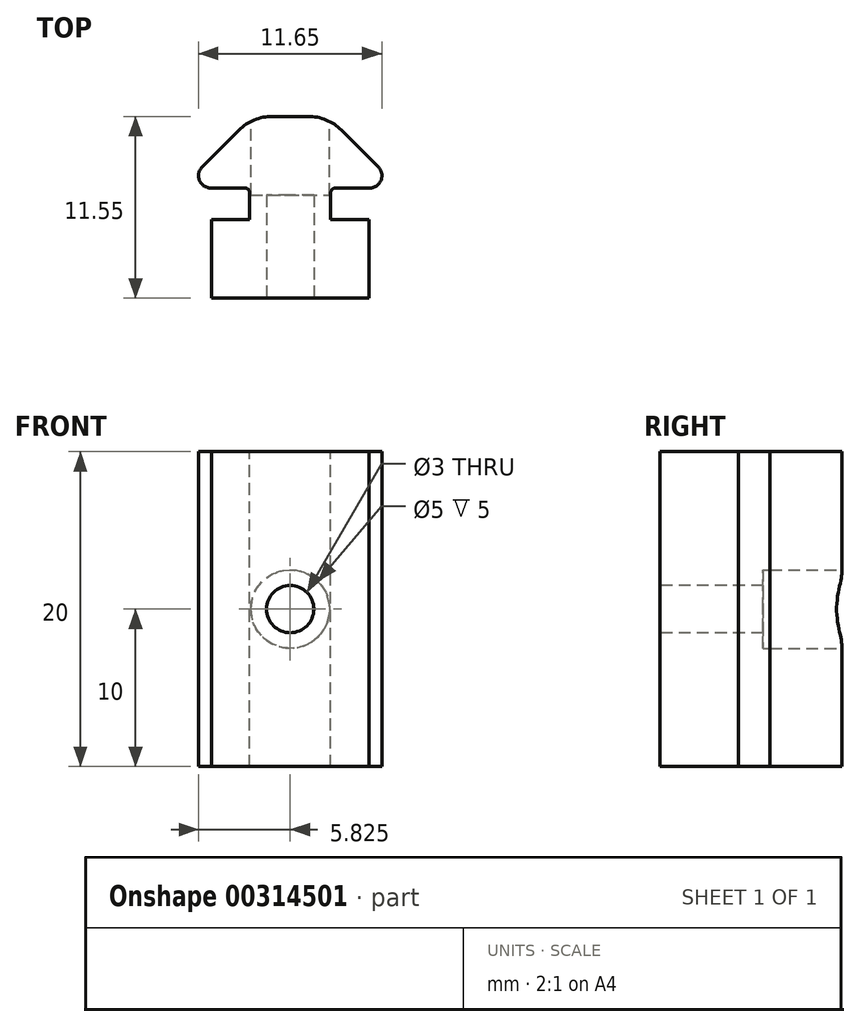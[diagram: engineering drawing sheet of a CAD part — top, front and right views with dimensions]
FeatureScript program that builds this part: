
annotation { "Feature Type Name" : "Feature", "Feature Type Description" : "" }
export const myFeature = defineFeature(function(context is Context, id is Id, definition is map)
    precondition{}
    {
        {
            var Q0;
            Q0=qCreatedBy(makeId("Top.planeOp"),FACE);
            var sketch = newSketch(context, id + "F0", { "sketchPlane" : qUnion([Q0])});
            skLineSegment(sketch, "E0.0.13", {"start": v(-0.8, -19.2) * mm, "end": v(-0.8, -18.5) * mm});
            skArc(sketch, "E0.0.14", {"start": v(-0.8, -18.5) * mm, "mid": v(-0.71, -18.29) * mm, "end": v(-0.5, -18.2) * mm});
            skLineSegment(sketch, "E0.0.15", {"start": v(-0.5, -18.2) * mm, "end": v(1.67, -18.2) * mm});
            skArc(sketch, "E0.0.16", {"start": v(1.67, -18.2) * mm, "mid": v(2.39, -17.72) * mm, "end": v(2.22, -16.87) * mm});
            skLineSegment(sketch, "E0.0.17", {"start": v(2.22, -16.87) * mm, "end": v(-0.12, -14.53) * mm});
            skArc(sketch, "E0.0.18", {"start": v(-0.12, -14.53) * mm, "mid": v(-1.1, -13.88) * mm, "end": v(-2.24, -13.65) * mm});
            skLineSegment(sketch, "E0.0.19", {"start": v(-2.24, -13.65) * mm, "end": v(-4.5, -13.65) * mm});
            skArc(sketch, "E0.0.20", {"start": v(-4.5, -13.65) * mm, "mid": v(-5.66, -13.88) * mm, "end": v(-6.63, -14.53) * mm});
            skLineSegment(sketch, "E0.0.21", {"start": v(-6.63, -14.53) * mm, "end": v(-8.97, -16.87) * mm});
            skArc(sketch, "E0.0.22", {"start": v(-8.97, -16.87) * mm, "mid": v(-9.14, -17.72) * mm, "end": v(-8.42, -18.2) * mm});
            skLineSegment(sketch, "E0.0.23", {"start": v(-8.42, -18.2) * mm, "end": v(-6.25, -18.2) * mm});
            skArc(sketch, "E0.0.24", {"start": v(-6.25, -18.2) * mm, "mid": v(-6.04, -18.29) * mm, "end": v(-5.95, -18.5) * mm});
            skLineSegment(sketch, "E0.0.25", {"start": v(-5.95, -18.5) * mm, "end": v(-5.95, -19.2) * mm});
            skLineSegment(sketch, "E1", {"start": v(-3.38, -13.65) * mm, "end": v(-3.38, -28.6) * mm, "construction": true});
            skLineSegment(sketch, "E2", {"start": v(-5.95, -19.2) * mm, "end": v(-5.95, -20.2) * mm});
            skLineSegment(sketch, "E3", {"start": v(-5.95, -20.2) * mm, "end": v(-8.38, -20.2) * mm});
            skLineSegment(sketch, "E4", {"start": v(-8.38, -20.2) * mm, "end": v(-8.38, -25.2) * mm});
            skLineSegment(sketch, "E5", {"start": v(-8.38, -25.2) * mm, "end": v(-3.38, -25.2) * mm});
            skLineSegment(sketch, "E6.MirrorCS", {"start": v(1.62, -25.2) * mm, "end": v(-3.38, -25.2) * mm});
            skLineSegment(sketch, "E7.MirrorCS", {"start": v(1.62, -20.2) * mm, "end": v(1.62, -25.2) * mm});
            skLineSegment(sketch, "E8.MirrorCS", {"start": v(-0.8, -19.2) * mm, "end": v(-0.8, -20.2) * mm});
            skLineSegment(sketch, "E9.MirrorCS", {"start": v(-0.8, -20.2) * mm, "end": v(1.62, -20.2) * mm});
            skSolve(sketch);
        }
        {
            var Q0;
            Q0=qSketchRegion(id+"F0",true);
            extrude(context, id + "F1", {"entities" : qUnion([Q0]), "oppositeDirection" : true, "depth" : 60 * mm});
        }
        {
            var Q0;
            Q0=makeQuery(id+"F1.opExtrude","SWEPT_FACE",FACE,{"disambiguationData":[OSD([sQuery(id+"F0.wireOp",EDGE,"E5"),sQuery(id+"F0.wireOp",EDGE,"E6.MirrorCS")])]});
            var sketch = newSketch(context, id + "F2", { "sketchPlane" : qUnion([Q0])});
            skLineSegment(sketch, "E10", {"start": v(-3.38, 0) * mm, "end": v(-3.38, -60) * mm, "construction": true});
            skCircle(sketch, "E11", {"center": v(-3.38, -50) * mm, "radius": 1.5 * mm});
            skCircle(sketch, "E12", {"center": v(-3.38, -30) * mm, "radius": 1.5 * mm});
            skCircle(sketch, "E13", {"center": v(-3.38, -10) * mm, "radius": 1.5 * mm});
            skSolve(sketch);
        }
        {
            var Q0;
            Q0=qSketchRegion(id+"F2",true);
            extrude(context, id + "F3", {"entities" : qUnion([Q0]), "operationType" : NewBodyOperationType.REMOVE, "oppositeDirection" : true, "depth" : 25 * mm});
        }
        {
            var Q0;
            Q0=makeQuery(id+"F3.boolean.opBoolean","SPLIT",FACE,{"disambiguationData":[TD([makeQuery(id+"F1.opExtrude","SWEPT_FACE",FACE,{"disambiguationData":[OSD([sQuery(id+"F0.wireOp",EDGE,"E0.0.18")])]}),makeQuery(id+"F1.opExtrude","SWEPT_FACE",FACE,{"disambiguationData":[OSD([sQuery(id+"F0.wireOp",EDGE,"E0.0.20")])]}),makeQuery(id+"F3.opExtrude","SWEPT_FACE",FACE,{"disambiguationData":[OSD([sQuery(id+"F2.wireOp",EDGE,"E12")])]}),makeQuery(id+"F3.opExtrude","SWEPT_FACE",FACE,{"disambiguationData":[OSD([sQuery(id+"F2.wireOp",EDGE,"E13")])]})])],"derivedFrom":makeQuery(id+"F1.opExtrude","SWEPT_FACE",FACE,{"disambiguationData":[OSD([sQuery(id+"F0.wireOp",EDGE,"E0.0.19")])]})});
            var sketch = newSketch(context, id + "F4", { "sketchPlane" : qUnion([Q0])});
            skCircle(sketch, "E14", {"center": v(3.38, -10) * mm, "radius": 2.5 * mm});
            skCircle(sketch, "E15", {"center": v(3.38, -30) * mm, "radius": 2.5 * mm});
            skSolve(sketch);
        }
        {
            var Q0;
            {var subQ0=sQuery(id+"F0.wireOp",EDGE,"E0.0.20");var subQ1=sQuery(id+"F0.wireOp",EDGE,"E0.0.19");var subQ2=sQuery(id+"F0.wireOp",EDGE,"E0.0.18");Q0=makeQuery(id+"F3.boolean.opBoolean","SPLIT",FACE,{"disambiguationData":[TD([makeQuery(id+"F1.opExtrude","CAP_FACE",FACE,{"disambiguationData":[OSD([sQuery(id+"F0.wireOp",EDGE,"E0.0.13"),sQuery(id+"F0.wireOp",EDGE,"E0.0.14"),sQuery(id+"F0.wireOp",EDGE,"E0.0.15"),sQuery(id+"F0.wireOp",EDGE,"E0.0.16"),sQuery(id+"F0.wireOp",EDGE,"E0.0.17"),subQ2,subQ1,subQ0,sQuery(id+"F0.wireOp",EDGE,"E0.0.21"),sQuery(id+"F0.wireOp",EDGE,"E0.0.22"),sQuery(id+"F0.wireOp",EDGE,"E0.0.23"),sQuery(id+"F0.wireOp",EDGE,"E0.0.24"),sQuery(id+"F0.wireOp",EDGE,"E0.0.25"),sQuery(id+"F0.wireOp",EDGE,"E2"),sQuery(id+"F0.wireOp",EDGE,"E3"),sQuery(id+"F0.wireOp",EDGE,"E4"),sQuery(id+"F0.wireOp",EDGE,"E5"),sQuery(id+"F0.wireOp",EDGE,"E6.MirrorCS"),sQuery(id+"F0.wireOp",EDGE,"E7.MirrorCS"),sQuery(id+"F0.wireOp",EDGE,"E8.MirrorCS"),sQuery(id+"F0.wireOp",EDGE,"E9.MirrorCS")])],"isStart":false}),makeQuery(id+"F1.opExtrude","SWEPT_FACE",FACE,{"disambiguationData":[OSD([subQ2])]}),makeQuery(id+"F1.opExtrude","SWEPT_FACE",FACE,{"disambiguationData":[OSD([subQ0])]}),makeQuery(id+"F3.opExtrude","SWEPT_FACE",FACE,{"disambiguationData":[OSD([sQuery(id+"F2.wireOp",EDGE,"E11")])]})])],"derivedFrom":makeQuery(id+"F1.opExtrude","SWEPT_FACE",FACE,{"disambiguationData":[OSD([subQ1])]})});}
            var sketch = newSketch(context, id + "F5", { "sketchPlane" : qUnion([Q0])});
            skCircle(sketch, "E16", {"center": v(3.38, -50) * mm, "radius": 2.5 * mm});
            skSolve(sketch);
        }
        {
            var Q0;
            Q0=qSketchRegion(id+"F4",true);
            var Q1;
            Q1=qSketchRegion(id+"F5",true);
            extrude(context, id + "F6", {"entities" : qUnion([Q0, Q1]), "operationType" : NewBodyOperationType.REMOVE, "oppositeDirection" : true, "depth" : 5 * mm});
        }
        {
            var Q0;
            Q0=makeQuery(id+"F1.opExtrude","CAP_FACE",FACE,{"disambiguationData":[OSD([sQuery(id+"F0.wireOp",EDGE,"E0.0.13"),sQuery(id+"F0.wireOp",EDGE,"E0.0.14"),sQuery(id+"F0.wireOp",EDGE,"E0.0.15"),sQuery(id+"F0.wireOp",EDGE,"E0.0.16"),sQuery(id+"F0.wireOp",EDGE,"E0.0.17"),sQuery(id+"F0.wireOp",EDGE,"E0.0.18"),sQuery(id+"F0.wireOp",EDGE,"E0.0.19"),sQuery(id+"F0.wireOp",EDGE,"E0.0.20"),sQuery(id+"F0.wireOp",EDGE,"E0.0.21"),sQuery(id+"F0.wireOp",EDGE,"E0.0.22"),sQuery(id+"F0.wireOp",EDGE,"E0.0.23"),sQuery(id+"F0.wireOp",EDGE,"E0.0.24"),sQuery(id+"F0.wireOp",EDGE,"E0.0.25"),sQuery(id+"F0.wireOp",EDGE,"E2"),sQuery(id+"F0.wireOp",EDGE,"E3"),sQuery(id+"F0.wireOp",EDGE,"E4"),sQuery(id+"F0.wireOp",EDGE,"E5"),sQuery(id+"F0.wireOp",EDGE,"E6.MirrorCS"),sQuery(id+"F0.wireOp",EDGE,"E7.MirrorCS"),sQuery(id+"F0.wireOp",EDGE,"E8.MirrorCS"),sQuery(id+"F0.wireOp",EDGE,"E9.MirrorCS")])],"isStart":true});
            extrude(context, id + "F7", {"entities" : qUnion([Q0]), "operationType" : NewBodyOperationType.REMOVE, "oppositeDirection" : true, "depth" : 40 * mm});
        }
    });
